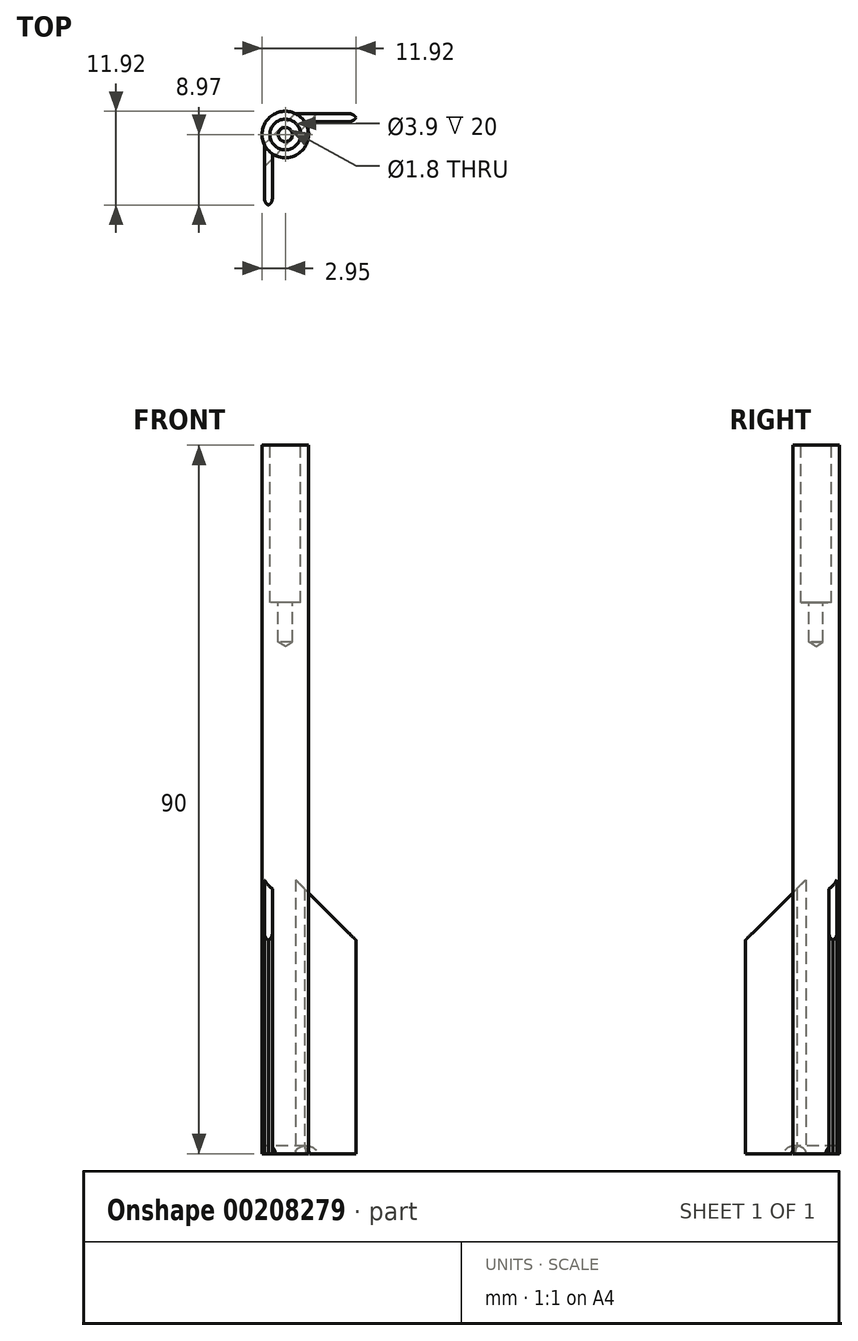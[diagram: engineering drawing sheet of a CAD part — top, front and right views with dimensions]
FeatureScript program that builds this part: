
annotation { "Feature Type Name" : "Feature", "Feature Type Description" : "" }
export const myFeature = defineFeature(function(context is Context, id is Id, definition is map)
    precondition{}
    {
        {
            var Q0;
            Q0=qCreatedBy(makeId("Top.planeOp"),FACE);
            var sketch = newSketch(context, id + "F0", { "sketchPlane" : qUnion([Q0])});
            skCircle(sketch, "E0", {"center": v(0, 0) * mm, "radius": 2.95 * mm});
            skSolve(sketch);
        }
        {
            var Q0;
            Q0 = qSketchRegion(id + "F0", true);
            extrude(context, id + "F1", {"entities" : qUnion([Q0]), "depth" : 95 * mm});
        }
        {
            var Q0;
            Q0=qCreatedBy(makeId("Top.planeOp"),FACE);
            var sketch = newSketch(context, id + "F2", { "sketchPlane" : qUnion([Q0])});
            skLineSegment(sketch, "E1.bottom", {"start": v(2.45, 1.65) * mm, "end": v(9.1, 1.65) * mm});
            skLineSegment(sketch, "E1.top", {"start": v(1.3, 2.65) * mm, "end": v(9.1, 2.65) * mm});
            skLineSegment(sketch, "E1.right", {"start": v(9.1, 1.65) * mm, "end": v(9.1, 2.65) * mm});
            skLineSegment(sketch, "E2.top", {"start": v(-1.65, -9.1) * mm, "end": v(-2.65, -9.1) * mm});
            skLineSegment(sketch, "E2.left", {"start": v(-1.65, -2.45) * mm, "end": v(-1.65, -9.1) * mm});
            skLineSegment(sketch, "E2.right", {"start": v(-2.65, -1.3) * mm, "end": v(-2.65, -9.1) * mm});
            skLineSegment(sketch, "E3", {"start": v(0.52, 4.7) * mm, "end": v(-4.71, -0.54) * mm, "construction": true});
            skLineSegment(sketch, "E4", {"start": v(2.24, 3.58) * mm, "end": v(-3.59, -2.24) * mm, "construction": true});
            skLineSegment(sketch, "E5", {"start": v(0, 0) * mm, "end": v(0, 6.73) * mm, "construction": true});
            skLineSegment(sketch, "E6", {"start": v(1.3, 2.65) * mm, "end": v(2.45, 1.65) * mm});
            skLineSegment(sketch, "E7", {"start": v(-2.65, -1.3) * mm, "end": v(-1.65, -2.45) * mm});
            skSolve(sketch);
        }
        {
            var Q0;
            Q0 = qSketchRegion(id + "F2", true);
            extrude(context, id + "F3", {"entities" : qUnion([Q0]), "operationType" : NewBodyOperationType.ADD, "depth" : 35 * mm});
        }
        {
            var Q0;
            Q0=makeQuery(id+"F3.opExtrude","CAP_EDGE",EDGE,{"disambiguationData":[OSD([sQuery(id+"F2.wireOp",EDGE,"E1.right")])],"isStart":false});
            var Q1;
            Q1=makeQuery(id+"F3.opExtrude","CAP_EDGE",EDGE,{"disambiguationData":[OSD([sQuery(id+"F2.wireOp",EDGE,"E2.top")])],"isStart":false});
            chamfer(context, id + "F4", {"entities" : qUnion([Q0, Q1]), "width" : 8 * mm, "tangentPropagation" : true});
        }
        {
            var Q0;
            Q0=makeQuery(id+"F3.opExtrude","SWEPT_EDGE",EDGE,{"disambiguationData":[OSD([sQuery(id+"F2.wireOp",EDGE,"E2.bottom"),sQuery(id+"F2.wireOp",EDGE,"E2.right")])]});
            var Q1;
            Q1=makeQuery(id+"F3.opExtrude","SWEPT_EDGE",EDGE,{"disambiguationData":[OSD([sQuery(id+"F2.wireOp",EDGE,"E2.bottom"),sQuery(id+"F2.wireOp",EDGE,"E2.left")])]});
            var Q2;
            Q2=makeQuery(id+"F3.opExtrude","SWEPT_EDGE",EDGE,{"disambiguationData":[OSD([sQuery(id+"F2.wireOp",EDGE,"E1.bottom"),sQuery(id+"F2.wireOp",EDGE,"E1.left")])]});
            var Q3;
            Q3=makeQuery(id+"F3.opExtrude","SWEPT_EDGE",EDGE,{"disambiguationData":[OSD([sQuery(id+"F2.wireOp",EDGE,"E1.top"),sQuery(id+"F2.wireOp",EDGE,"E1.left")])]});
            fillet(context, id + "F5", {"entities" : qUnion([Q0, Q1, Q2, Q3]), "radius" : 1 * mm, "tangentPropagation" : true, "allowEdgeOverflow" : false});
        }
        {
            var Q0;
            Q0=qCreatedBy(makeId("Top.planeOp"),FACE);
            var sketch = newSketch(context, id + "F6", { "sketchPlane" : qUnion([Q0])});
            skLineSegment(sketch, "E8", {"start": v(0, 0) * mm, "end": v(-25.4, 0) * mm, "construction": true});
            skLineSegment(sketch, "E9", {"start": v(-25.4, 0) * mm, "end": v(-25.4, 25.4) * mm, "construction": true});
            skLineSegment(sketch, "E10", {"start": v(0, 0) * mm, "end": v(-25.4, 25.4) * mm, "construction": true});
            skSolve(sketch);
        }
        {
            var Q0;
            Q0=qCreatedBy(makeId("Right.planeOp"),FACE);
            var sketch = newSketch(context, id + "F7", { "sketchPlane" : qUnion([Q0])});
            skLineSegment(sketch, "E11", {"start": v(0, 0) * mm, "end": v(0, 29.42) * mm, "construction": true});
            skSolve(sketch);
        }
        {
            var Q0;
            Q0=sQuery(id+"F7.wireOp",VERTEX,"E11.end");
            var Q1;
            Q1=sQuery(id+"F7.wireOp",VERTEX,"E11.start");
            var Q2;
            Q2=sQuery(id+"F6.wireOp",VERTEX,"E10.end");
            cPlane(context, id + "F8", {"entities" : qUnion([Q0, Q1, Q2]), "cplaneType" : CPlaneType.THREE_POINT, "offset" : 25 * mm, "width" : 150 * mm, "height" : 150 * mm});
        }
        {
            var Q0;
            Q0=qCreatedBy(id+"F8.planeOp",FACE);
            var sketch = newSketch(context, id + "F9", { "sketchPlane" : qUnion([Q0])});
            skCircle(sketch, "E12", {"center": v(0, 0) * mm, "radius": 1 * mm});
            skSolve(sketch);
        }
        {
            var Q0;
            Q0 = qSketchRegion(id + "F9", true);
            extrude(context, id + "F10", {"entities" : qUnion([Q0]), "operationType" : NewBodyOperationType.REMOVE, "endBound" : BoundingType.SYMMETRIC, "oppositeDirection" : true, "depth" : 25 * mm});
        }
        {
            var Q0;
            Q0=makeQuery(id+"FTPy9lgln27TIuH_1.boolean.opBoolean","SPLIT",FACE,{"disambiguationData":[TD([makeQuery(id+"FTPy9lgln27TIuH_1.opExtrude","SWEPT_FACE",FACE,{"disambiguationData":[OSD([sQuery(id+"FhPtBav8R8S2ktQ_1.wireOp",EDGE,"FGYnKAy6-05tA-UzEH-cDNn-WpqFilacSDBv")])]})])],"derivedFrom":makeQuery(id+"F1.opExtrude","CAP_FACE",FACE,{"disambiguationData":[OSD([sQuery(id+"F0.wireOp",EDGE,"E0")])],"isStart":false})});
            extrude(context, id + "F11", {"entities" : qUnion([Q0]), "operationType" : NewBodyOperationType.REMOVE, "oppositeDirection" : true, "depth" : 5 * mm});
        }
        {
            var Q0;
            Q0=makeQuery(id+"F11.boolean.opBoolean","COPY",FACE,{"derivedFrom":makeQuery(id+"F11.opExtrude","CAP_FACE",FACE,{"disambiguationData":[OSD([sQuery(id+"F0.wireOp",EDGE,"E0")])],"isStart":false})});
            var sketch = newSketch(context, id + "F12", { "sketchPlane" : qUnion([Q0])});
            skCircle(sketch, "E13", {"center": v(0, 0) * mm, "radius": 1.95 * mm});
            skSolve(sketch);
        }
        {
            var Q0;
            Q0 = qSketchRegion(id + "F12", true);
            extrude(context, id + "F13", {"entities" : qUnion([Q0]), "operationType" : NewBodyOperationType.REMOVE, "oppositeDirection" : true, "depth" : 20 * mm});
        }
        {
            var Q0;
            Q0=makeQuery(id+"F13.boolean.opBoolean","COPY",FACE,{"derivedFrom":makeQuery(id+"F13.opExtrude","CAP_FACE",FACE,{"disambiguationData":[OSD([sQuery(id+"F12.wireOp",EDGE,"E13")])],"isStart":false})});
            var sketch = newSketch(context, id + "F14", { "sketchPlane" : qUnion([Q0])});
            skPoint(sketch, "E14.0", {"position": v(0, 0) * mm});
            skSolve(sketch);
        }
        {
            var Q0;
            Q0=sQuery(id+"F14.wireOp",VERTEX,"E14.0");
            var Q1;
            Q1=makeQuery(id+"F1.opExtrude","SWEPT_BODY",BODY,{"disambiguationData":[OSD([sQuery(id+"F0.wireOp",EDGE,"E0")])]});
            hole(context, id + "F15", {"style" : HoleStyle.SIMPLE, "endStyle" : HoleEndStyle.BLIND, "holeDiameter" : 1.8 * mm, "holeDepth" : 5 * mm, "locations" : qUnion([Q0]), "scope" : qUnion([Q1])});
        }
    });
